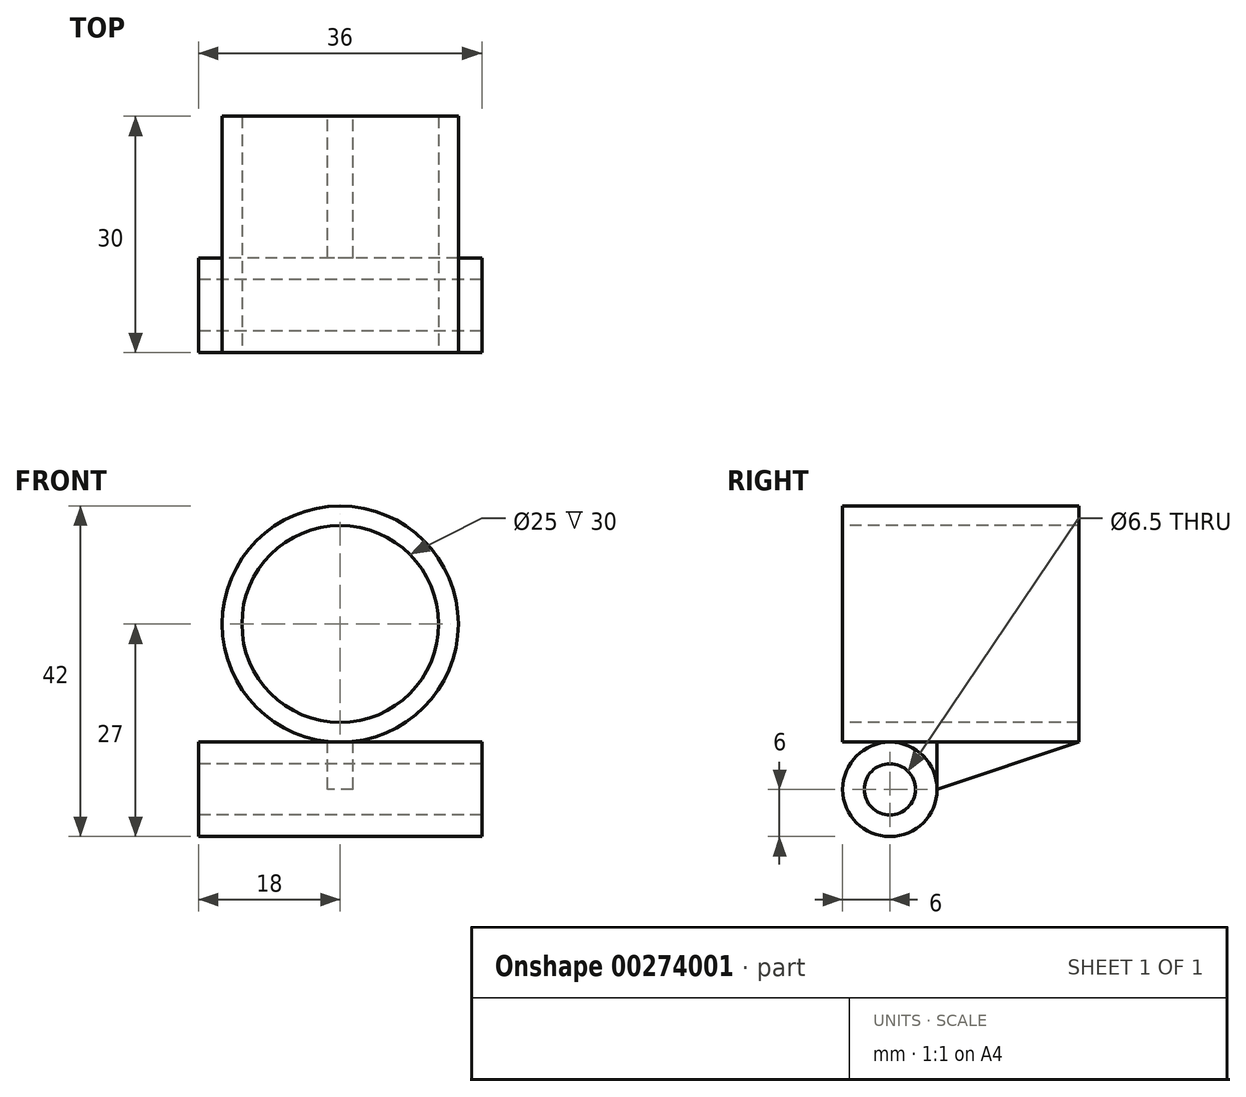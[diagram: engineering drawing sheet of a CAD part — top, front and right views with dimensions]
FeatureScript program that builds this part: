
annotation { "Feature Type Name" : "Feature", "Feature Type Description" : "" }
export const myFeature = defineFeature(function(context is Context, id is Id, definition is map)
    precondition{}
    {
        {
            var Q0;
            Q0=qCreatedBy(makeId("Front.planeOp"),FACE);
            var sketch = newSketch(context, id + "F0", { "sketchPlane" : qUnion([Q0])});
            skCircle(sketch, "E0", {"center": v(0, 15) * mm, "radius": 15 * mm});
            skCircle(sketch, "E1", {"center": v(0, 15) * mm, "radius": 12.5 * mm});
            skSolve(sketch);
        }
        {
            var Q0;
            Q0=qSketchRegion(id+"F0",true);
            extrude(context, id + "F1", {"entities" : qUnion([Q0]), "oppositeDirection" : true, "depth" : 30 * mm});
        }
        {
            var Q0;
            Q0=qCreatedBy(makeId("Right.planeOp"),FACE);
            var sketch = newSketch(context, id + "F2", { "sketchPlane" : qUnion([Q0])});
            skCircle(sketch, "E2", {"center": v(6, -6) * mm, "radius": 6 * mm});
            skLineSegment(sketch, "E3", {"start": v(0, 0) * mm, "end": v(30, 0) * mm});
            skLineSegment(sketch, "E4", {"start": v(0, 0) * mm, "end": v(0, -17.95) * mm});
            skCircle(sketch, "E5", {"center": v(6, -6) * mm, "radius": 3.25 * mm});
            skSolve(sketch);
        }
        {
            var Q0;
            Q0=makeQuery(id+"F2.imprint","IMPRINT",FACE,{"disambiguationData":[TD([[makeQuery(id+"F2.imprint","IMPRINT",EDGE,{"derivedFrom":sQuery(id+"F2.wireOp",EDGE,"E5")}),-1.0]])]});
            extrude(context, id + "F3", {"entities" : qUnion([Q0]), "endBound" : BoundingType.SYMMETRIC, "depth" : 36 * mm});
        }
        {
            var Q0;
            Q0=qCreatedBy(makeId("Right.planeOp"),FACE);
            var sketch = newSketch(context, id + "F4", { "sketchPlane" : qUnion([Q0])});
            skLineSegment(sketch, "E6", {"start": v(0, 0) * mm, "end": v(30, 0) * mm});
            skLineSegment(sketch, "E7", {"start": v(30, 30) * mm, "end": v(0, 30) * mm});
            skCircle(sketch, "E8.0", {"center": v(6, -6) * mm, "radius": 6 * mm});
            skLineSegment(sketch, "E9", {"start": v(30, 0) * mm, "end": v(12, -6) * mm});
            skLineSegment(sketch, "E10", {"start": v(12, -6) * mm, "end": v(12, 0) * mm});
            skSolve(sketch);
        }
        {
            var Q0;
            {var subQ0=sQuery(id+"F4.wireOp",EDGE,"E9");Q0=makeQuery(id+"F4.imprint","IMPRINT",FACE,{"disambiguationData":[TD([[makeQuery(id+"F4.imprint","IMPRINT",EDGE,{"derivedFrom":subQ0}),-1.0]])]});}
            extrude(context, id + "F5", {"entities" : qUnion([Q0]), "endBound" : BoundingType.SYMMETRIC, "depth" : 3.2 * mm});
        }
    });
